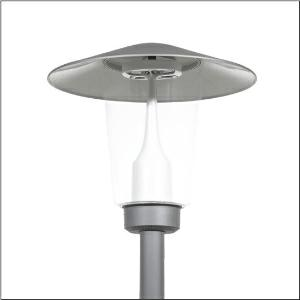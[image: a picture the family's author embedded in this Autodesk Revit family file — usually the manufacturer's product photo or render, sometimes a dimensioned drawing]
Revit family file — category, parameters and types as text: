
# Revit family: pilzleuchte_iq___p1_0a_5xa5235ff14hp_c3dc
name_source: partatom
category: Lighting Fixtures
units: mm (PartAtom-declared; Revit-internal decimal feet)

## family parameters
Cut with Voids When Loaded = No
Host = Face
Light Source = No
Part Type = Normal
Room Calculation Point = No
Round Connector Dimension = Use Diameter
Shared = No

## types (1)
- --- (1 x LED, 4740 lm, 33.6 W, 3000K)
    Apparent Load = 34 VA
    CIE Flux Codes = 35 64 90 96 100
    Color Rendering = 70
    Color Temperature = 3000K
    Default Elevation = 1800 mm
    Description = Mushroom Luminaire iQ, mast luminaire, Module 540 iQ-SR, primary light control with 3 zone facetted reflector, of plastic, silver coated, highly specular, structured, primary optical cover: cover, of PMMA, transparent, light distribution: P1.0a, light emission: direct distribution, primary light characteristic: strongly asymmetric, installation type: post-top, LED, High Power LED, rated luminous flux: 4.740lm, luminous efficacy: 141lm/W, light colour: 730, colour temperature: 3000K, control gear: ECG iQ, control: pre-setting: logarithmic dimming characteristic, Street-Remote, Auto-Match, Temp-Guard, Lumen-Switch, Night-Set, Smart-Wire, Light-Fading, Desk-Remote (wireless, voltage-free reading and setting of iQ features in the workshop via application-optimized NFC function/RFID function), optimised constant luminous flux control (CLO 2.0), with terminal, 6-pole, max. 2.5mm², mains connection: 230..240V, AC, 50/60Hz, start of lifetime: 34W, end of service life: 36W, reduction: 15W, luminaire housing, upper part, of glass-fibre reinforced polyester, coated, Siteco® metallic grey (DB 702S), diameter: 650mm, height: 586mm, spigot size: d x l = 76 x 70mm (post-top) | with reducer (optional accessory) 60 x 70mm, post-top mast mounting element, of diecast aluminium, coated, Siteco® metallic grey (DB 702S), Module 540 iQ-SR, traffic white (RAL 9016), equipment: Power, protection rating (complete): IP65, insulation class (complete): insulation class II (safety insulation), certification: CE, ENEC, VDE, packaging unit: 1 piece

Light Distribution: P1.0a
    Height = 586 mm
    Lamp = 1 x LED
    Lamp Light Flux = 4740 lm
    Lamp Power = 33.6 W
    Lamp count = 1
    Length = 650 mm
    Luminous efficacy = 141 lm/W
    Manufacturer = Siteco
    ModVariant = No
    Model = 5XA5235FF14HP
    Number of Poles = 1
    OnlyDefault = Yes
    Power Factor = 1
    Product Name = Pilzleuchte iQ | P1.0a
    Product group = mast luminaire | pylon top
    ProductGroupID = 6100
    Protection Class = Protection class II
    Protection Degree = IP 65
    RLX_Detail_Level = 1
    RLX_Emergency_Light_Flux = 0 lm
    RLX_Emergency_Type = 0
    RLX_Emergency_Type_DB = No
    RlxData = <blob elided: 52005 chars, md5=858a48ae>
    Socket = socket
    Standby Power = 0 W
    System Light Flux = 4740 lm
    System Power = 34 W
    Type Comments = factory setting: luminous flux: 100 % | dim-lin: 254 | 695 mA
    Type Image = l_1006077.jpg
    URL = http://relux.com
    VarID = @adj_164829
    Voltage = 0 V
    Weight = 0.00 kg
    Width = 0 mm  [stored 0 ft]

note: [stored X ft] marks values corroborated as IEEE doubles in the binary element streams (Revit-internal decimal feet)

## geometry (parser evidence)
native form markers: Blend x4, Sweep x13
no freeform markers — native parametric forms only
